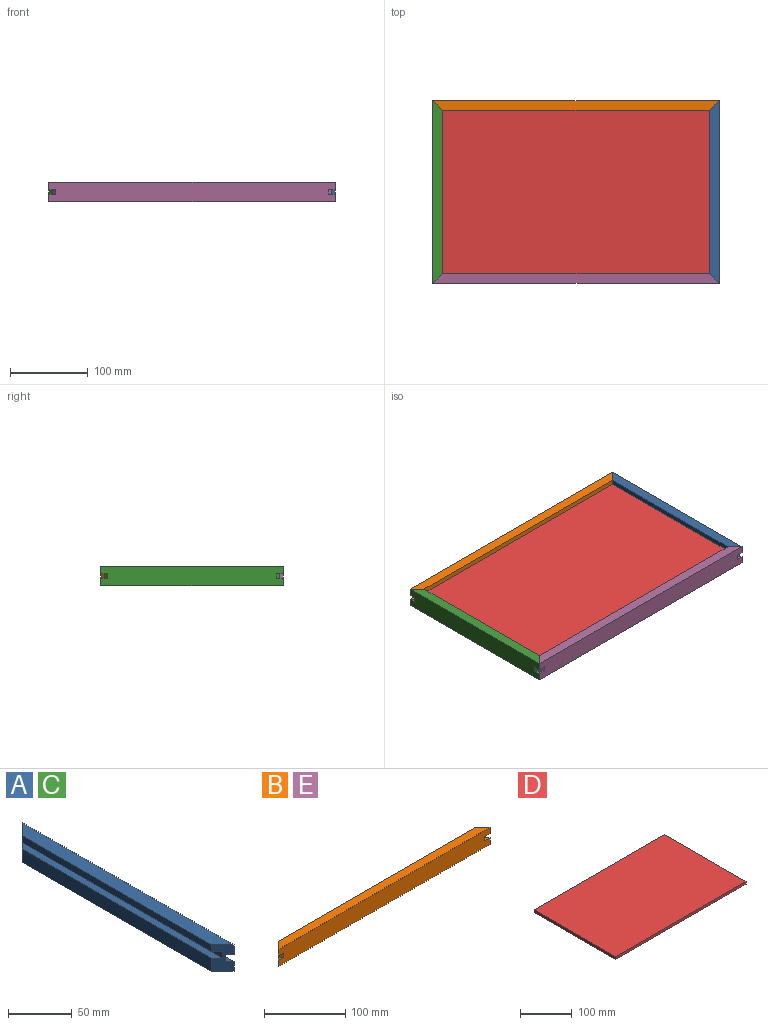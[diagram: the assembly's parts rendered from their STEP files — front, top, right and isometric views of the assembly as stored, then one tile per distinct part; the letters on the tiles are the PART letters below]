
ASSEMBLY  parts=5 mates=1
PART A: 16 faces, bbox 12.7x235x25.4 mm
  f0: plane 25.4x12.7mm, normal (-0.71,0.71,0), area 358.8mm2, adj f1,f3,f4,f5,f6,f7,f8,f9
  f1: plane 234.95x25.4mm, normal (1,0,0), area 5853.7mm2, adj f0,f2,f4,f6,f10,f11,f12,f13
  f2: plane 25.4x12.7mm, normal (-0.71,-0.71,0), area 358.8mm2, adj f1,f3,f4,f5,f6,f7,f8,f9
  f3: plane 209.55x6.35mm, normal (-1,0,0), area 1330.6mm2, adj f0,f2,f4,f8
  f4: plane 234.95x12.7mm, normal (0,0,1), area 2822.6mm2, adj f0,f1,f2,f3
  f5: plane 209.55x12.7mm, normal (-1,0,0), area 2661.3mm2, adj f0,f2,f6,f7
  f6: plane 234.95x12.7mm, normal (0,0,-1), area 2822.6mm2, adj f0,f1,f2,f5
  f7: plane 222.25x6.35mm, normal (0,0,1), area 1371mm2, adj f0,f2,f5,f9
  f8: plane 222.25x6.35mm, normal (0,0,-1), area 1371mm2, adj f0,f2,f3,f9
  f9: plane 222.25x6.35mm, normal (-1,0,0), area 1411.3mm2, adj f0,f2,f7,f8
  f10: plane 8.98x4.49mm, normal (0,0,1), area 20.2mm2, adj f1,f2,f12
  f11: plane 8.98x4.49mm, normal (0,0,-1), area 20.2mm2, adj f1,f2,f12
  f12: plane 6.35x4.49mm, normal (0.71,-0.71,0), area 40.3mm2, adj f1,f2,f10,f11
  f13: plane 8.98x4.49mm, normal (0,0,1), area 20.2mm2, adj f0,f1,f14
  f14: plane 6.35x4.49mm, normal (0.71,0.71,0), area 40.3mm2, adj f0,f1,f13,f15
  f15: plane 8.98x4.49mm, normal (0,0,-1), area 20.2mm2, adj f0,f1,f14
PART B: 16 faces, bbox 368.3x12.7x25.4 mm
  f0: plane 368.3x25.4mm, normal (0,-1,0), area 9240.8mm2, adj f1,f2,f4,f6,f10,f11,f12,f13
  f1: plane 25.4x12.7mm, normal (-0.71,0.71,0), area 358.8mm2, adj f0,f3,f4,f5,f6,f7,f8,f9
  f2: plane 25.4x12.7mm, normal (0.71,0.71,0), area 358.8mm2, adj f0,f3,f4,f5,f6,f7,f8,f9
  f3: plane 342.9x6.35mm, normal (0,1,0), area 2177.4mm2, adj f1,f2,f4,f8
  f4: plane 368.3x12.7mm, normal (0,0,1), area 4516.1mm2, adj f0,f1,f2,f3
  f5: plane 342.9x12.7mm, normal (0,1,0), area 4354.8mm2, adj f1,f2,f6,f7
  f6: plane 368.3x12.7mm, normal (0,0,-1), area 4516.1mm2, adj f0,f1,f2,f5
  f7: plane 355.6x6.35mm, normal (0,0,1), area 2217.7mm2, adj f1,f2,f5,f9
  f8: plane 355.6x6.35mm, normal (0,0,-1), area 2217.7mm2, adj f1,f2,f3,f9
  f9: plane 355.6x6.35mm, normal (0,1,0), area 2258.1mm2, adj f1,f2,f7,f8
  f10: plane 8.98x4.49mm, normal (0,0,1), area 20.2mm2, adj f0,f2,f11
  f11: plane 6.35x4.49mm, normal (0.71,-0.71,0), area 40.3mm2, adj f0,f2,f10,f12
  f12: plane 8.98x4.49mm, normal (0,0,-1), area 20.2mm2, adj f0,f2,f11
  f13: plane 8.98x4.49mm, normal (0,0,1), area 20.2mm2, adj f0,f1,f15
  f14: plane 8.98x4.49mm, normal (0,0,-1), area 20.2mm2, adj f0,f1,f15
  f15: plane 6.35x4.49mm, normal (-0.71,-0.71,0), area 40.3mm2, adj f0,f1,f13,f14
PART C: same geometry as A
PART D: 6 faces, bbox 355.6x222.3x6.4 mm
  f0: plane 355.6x6.35mm, normal (0,1,0), area 2258.1mm2, adj f1,f3,f4,f5
  f1: plane 222.25x6.35mm, normal (-1,0,0), area 1411.3mm2, adj f0,f2,f4,f5
  f2: plane 355.6x6.35mm, normal (0,-1,0), area 2258.1mm2, adj f1,f3,f4,f5
  f3: plane 222.25x6.35mm, normal (1,0,0), area 1411.3mm2, adj f0,f2,f4,f5
  f4: plane 355.6x222.25mm, normal (0,0,1), area 79032.1mm2, adj f0,f1,f2,f3
  f5: plane 355.6x222.25mm, normal (0,0,-1), area 79032.1mm2, adj f0,f1,f2,f3
PART E: same geometry as B
PLACE A t=(171.45,104.78,76.2)mm
PLACE B rot(axis=(0,0,1),180deg) t=(0,209.55,76.2)mm
PLACE C rot(axis=(0,0,1),180deg) t=(-171.45,104.78,76.2)mm
PLACE D rot(axis=(-0.31,-0.15,-0.94),0deg) t=(0,104.78,88.9)mm
PLACE E t=(0,0,76.2)mm
MATE planar D.f4 <-> C.f8  axis (0,0,1) through (-177.8,-6.35,95.25)mm
